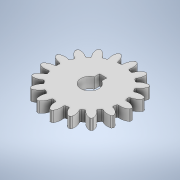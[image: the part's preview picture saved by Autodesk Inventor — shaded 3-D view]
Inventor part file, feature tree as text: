
AUTODESK INVENTOR PART (.ipt)
format: ipt  version: 2020 (Build 240168000, 168)  size: 302,080 bytes
history: native  units: mm
features: extrude x2, sketch x2, fillet x1, pattern_circular x1
ambient origin geometry x8: Origin, YZ Plane, XZ Plane, XY Plane, X Axis, Y Axis, Z Axis, Center Point
bodies: Solid1 (feature_tree)
feature tree (6):
  extrude  "Extrusion1"  Depth=2.0mm
  fillet  "Fillet2"  Radius=2.0mm
  pattern_circular  "Circular Pattern2"  [2 undecoded]
  extrude  "Extrusion2"  Depth=0.4mm TaperAngle=360.0deg
  sketch  "Sketch1"  dims[d4=3.0mm d5=0.0mm d13=5.0mm d14=2.0mm]
  sketch  "Sketch2"  dims[d15=3.7mm d16=0.0mm d17=0.0mm d18=170.0mm d19=360.0deg d23=21.0mm d25=1.544118mm d26=1.235294mm d27=3.490659mm d28=19.733545mm d29=3.490659mm d30=0.308824mm d31=0.617647mm d32=0.9702mm d33=0.4mm]
note: 2 required parameter values undecoded (feature->parameter linkage not recoverable at this tier; creation-order binding heuristic only, values carry confidence <= 0.55)
